# Revit family: Fluid-Storage_Tank-Accessory_Xerxes_Inlet-Outlet
name_source: partatom
category: Generic Models
units: mm (PartAtom-declared; Revit-internal decimal feet)

## family parameters
Always vertical = No
Can host rebar = No
Classification Number = 23.65.20.11
Cut with Voids When Loaded = No
Maintain Annotation Orientation = No
Part Type = Normal
Room Calculation Point = No
Round Connector Dimension = Use Radius
Shared = No
Work Plane-Based = Yes

## types (6) — shared parameters
Assembly Code = G30
Construction Details = http://www.arcat.com
Default Elevation = 0' - 0"
Keynote = 13200
Manufacturer = Xerxes Corporation
Manufacturer Fax = 952-887-1882
Manufacturer Website = http://www.xerxes.com
Product Data = http://www.arcat.com
Revision = R1_2015-07
Sales Information = http://www.xerxes.com
SpecWizard = http://www.arcat.com
Specification = http://www.arcat.com
URL = http://www.xerxes.com
zero-valued in all types: Expected Lifespan (Years), Maintenance Schedule (Months), Warranty Duration (Years)

## per-type parameters (varying)
| type | Description | Model |
| Inspection Tube | Xerxes Tank Inspection Tube | Inspection Tube |
| Vent | Xerxes Tank Vent | Vent |
| Flanged Fluid Outlet | Xerxes Tank Flanged Fluid Outlet | Flanged Outlet |
| Fluid Outlet | Xerxes Tank Fluid Outlet | Outlet |
| Flanged Fluid Inlet | Xerxes Tank Flanged Fluid Inlet | Flanged Inlet |
| Fluid Inlet | Xerxes Tank Fluid Inlet | Inlet |

## geometry (parser evidence)
native form markers: Sweep x2
no freeform markers — native parametric forms only
